# Revit family: b30dc43a-8e02-4bed-93b3-0e71141fe447
name_source: partatom
category: Plumbing Fixtures
revit_build: Autodesk Revit 2016 (Build: 20161004_0715(x64)
units: mm (PartAtom-declared; Revit-internal decimal feet)

## family parameters
Cut with Voids When Loaded = No
Host = Face
OmniClass Number = 23.45.05.21.11
OmniClass Title = Water Closets
Part Type = Normal
Room Calculation Point = No
Round Connector Dimension = Use Diameter
Shared = No

## types (1)
- Not a Type - See Type Catalog
    ADA Compliant = Yes
    Assembly Code = D2010100
    CW Connection = Yes
    Cold Water Inlet = Cold Water Inlet
    Date Modified = 08/10/2018
    Default Elevation = 0"
    Finish = Default
    Flow Rate = 0 GPM
    Flush Rate = 1.6 GPF
    HW Connection = No
    Height = 31 1/4"
    Hot Water Inlet = Hot Water Inlet
    Left-hand trip lever = No
    Length = 30 1/8"
    Manufacturer = KOHLER Co.
    MasterFormat 1995 = 15410
    MasterFormat 2004 = 22.41.13
    Material = Vitreous China
    Pressure = 80.00 psi
    Product Documentation Link = http://www.us.kohler.com
    Product Name = Highline Classic
    Product Page URL = http://www.us.kohler.com
    Right-hand trip lever = No
    Rough-In = 12"
    Seat Included = No
    Type = 0
    URL = https://www.us.kohler.com
    Vent Connection = No
    Waste Connection = Yes
    Waste Water Outlet = Waste Water Outlet
    Width = 21 1/4"

## geometry (parser evidence)
native form markers: Sweep x5
no freeform markers — native parametric forms only
